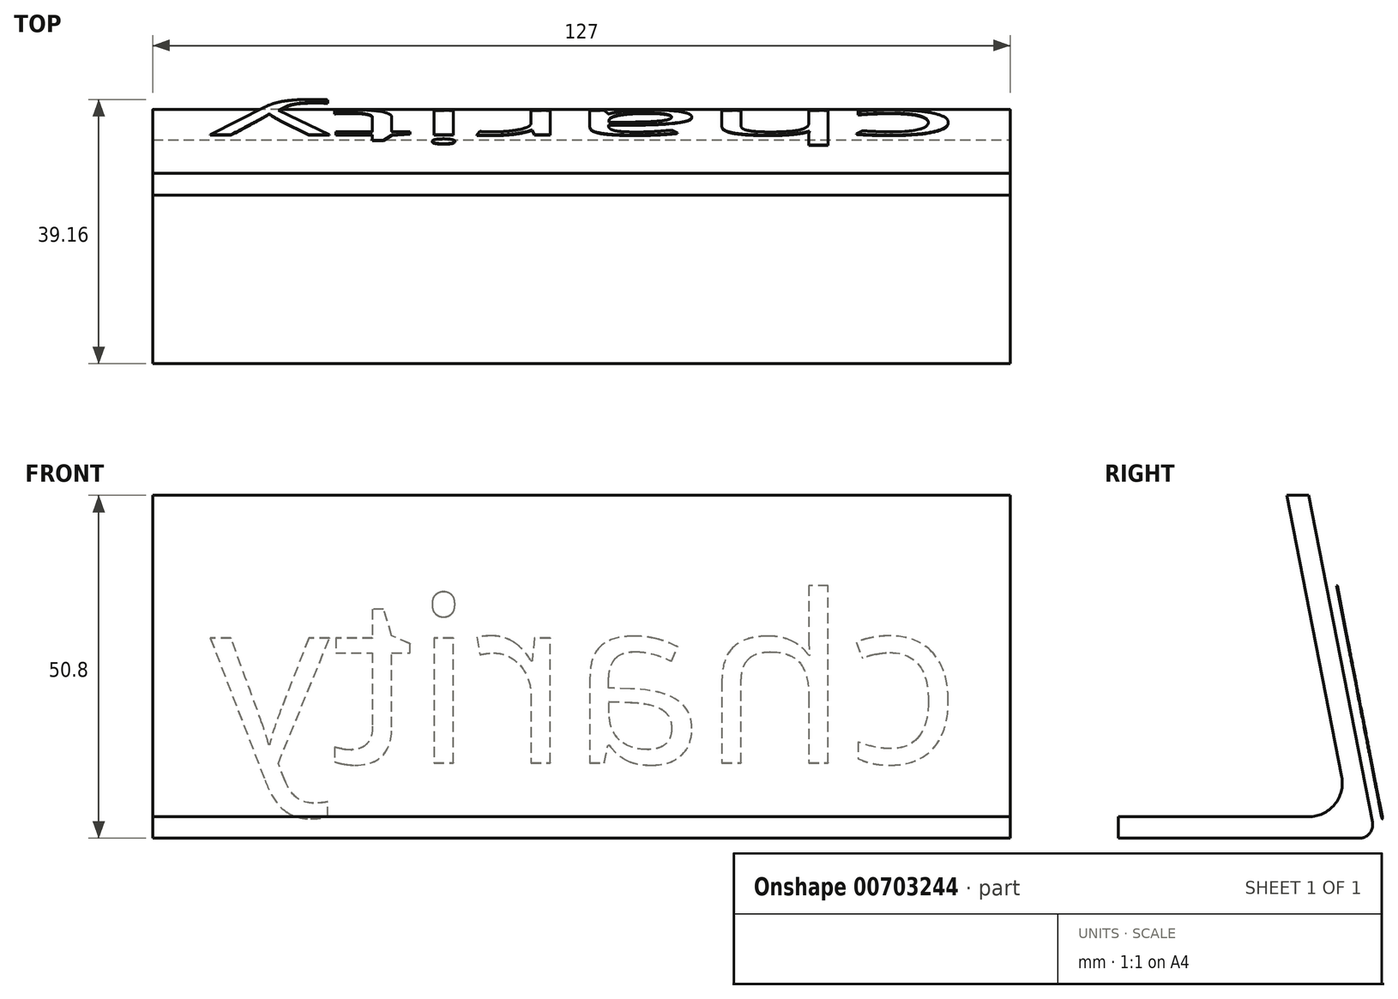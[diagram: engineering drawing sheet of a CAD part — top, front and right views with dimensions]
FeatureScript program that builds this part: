
annotation { "Feature Type Name" : "Feature", "Feature Type Description" : "" }
export const myFeature = defineFeature(function(context is Context, id is Id, definition is map)
    precondition{}
    {
        {
            var Q0;
            Q0=qCreatedBy(makeId("Right.planeOp"),FACE);
            var sketch = newSketch(context, id + "F0", { "sketchPlane" : qUnion([Q0])});
            skLineSegment(sketch, "E0", {"start": v(-20.53, 0) * mm, "end": v(17.57, 0) * mm});
            skLineSegment(sketch, "E1", {"start": v(17.57, 0) * mm, "end": v(7.67, 50.8) * mm});
            skLineSegment(sketch, "E2", {"start": v(7.67, 50.8) * mm, "end": v(4.44, 50.8) * mm});
            skLineSegment(sketch, "E3", {"start": v(4.44, 50.8) * mm, "end": v(13.72, 3.17) * mm});
            skLineSegment(sketch, "E4", {"start": v(13.72, 3.18) * mm, "end": v(-20.53, 3.17) * mm});
            skLineSegment(sketch, "E5", {"start": v(-20.53, 3.17) * mm, "end": v(-20.53, 0) * mm});
            skSolve(sketch);
        }
        {
            var Q0;
            Q0=makeQuery(id+"F0.imprint","IMPRINT",FACE,{"disambiguationData":[TD([[makeQuery(id+"F0.imprint","IMPRINT",EDGE,{"derivedFrom":sQuery(id+"F0.wireOp",EDGE,"E0")}),1.0]])]});
            extrude(context, id + "F1", {"entities" : qUnion([Q0]), "depth" : 127 * mm, "offsetDistance" : 25 * mm});
        }
        {
            var Q0;
            Q0=makeQuery(id+"F1.opExtrude","SWEPT_FACE",FACE,{"disambiguationData":[OSD([sQuery(id+"F0.wireOp",EDGE,"E1")])]});
            var sketch = newSketch(context, id + "F2", { "sketchPlane" : qUnion([Q0])});
            skText(sketch, "E6", { "text": "charity", "fontName": "OpenSans-Regular.ttf"});
            const initialGuessF2  = {"E6": [-0.1198, 0.00772, 1, 0, 0.02533]};
            skSetInitialGuess(sketch, initialGuessF2);
            skSolve(sketch);
        }
        {
            var Q0;
            Q0=makeQuery(id+"F2.imprint","IMPRINT",FACE,{"disambiguationData":[TD([[makeQuery(id+"F2.imprint","IMPRINT",EDGE,{"derivedFrom":sQuery(id+"F2.wireOp",EDGE,"9b1ba927-fd59-437d-b54f-c837bd06c2d1.sketch_text.stroke-0")}),-1.0]])]});
            var Q1;
            Q1 = qSketchRegion(id + "F2", true);
            extrude(context, id + "F3", {"entities" : qUnion([Q0, Q1]), "operationType" : NewBodyOperationType.ADD, "depth" : 1.59 * mm, "offsetDistance" : 25 * mm});
        }
        {
            var Q0;
            Q0=makeQuery(id+"F1.opExtrude","SWEPT_EDGE",EDGE,{"disambiguationData":[OSD([sQuery(id+"F0.wireOp",EDGE,"E3"),sQuery(id+"F0.wireOp",EDGE,"E4")])]});
            fillet(context, id + "F4", {"entities" : qUnion([Q0]), "radius" : 5 * mm, "tangentPropagation" : true, "allowEdgeOverflow" : false});
        }
        {
            var Q0;
            Q0=makeQuery(id+"F1.opExtrude","SWEPT_EDGE",EDGE,{"disambiguationData":[OSD([sQuery(id+"F0.wireOp",EDGE,"E0"),sQuery(id+"F0.wireOp",EDGE,"E1")])]});
            fillet(context, id + "F5", {"entities" : qUnion([Q0]), "radius" : 2 * mm, "tangentPropagation" : true, "allowEdgeOverflow" : false});
        }
        {
            var Q0;
            Q0 = qSketchRegion(id + "F2", true);
            extrude(context, id + "F6", {"entities" : qUnion([Q0]), "operationType" : NewBodyOperationType.REMOVE, "depth" : 1.5 * mm, "offsetDistance" : 25 * mm});
        }
    });
